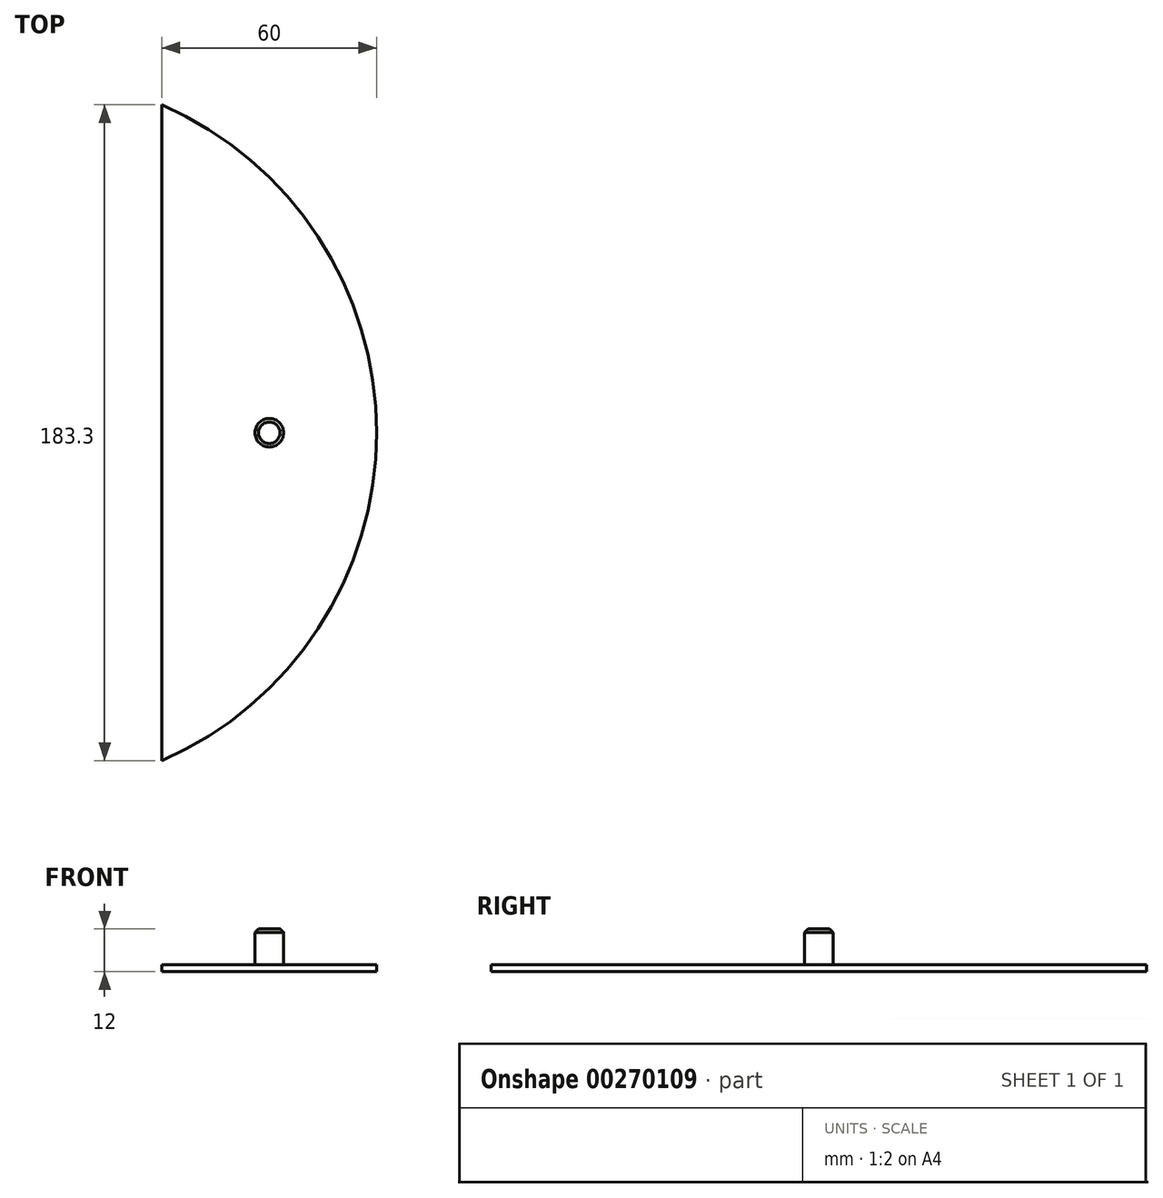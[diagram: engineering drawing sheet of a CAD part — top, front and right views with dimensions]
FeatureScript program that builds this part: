
annotation { "Feature Type Name" : "Feature", "Feature Type Description" : "" }
export const myFeature = defineFeature(function(context is Context, id is Id, definition is map)
    precondition{}
    {
        {
            var Q0;
            Q0=qCreatedBy(makeId("Top.planeOp"),FACE);
            var sketch = newSketch(context, id + "F0", { "sketchPlane" : qUnion([Q0])});
            skLineSegment(sketch, "E0.left", {"start": v(0, -100) * mm, "end": v(0, 100) * mm});
            skPoint(sketch, "E0.middle", {"position": v(0, 0) * mm});
            skArc(sketch, "E1", {"start": v(0, -100) * mm, "mid": v(100, 0) * mm, "end": v(0, 100) * mm});
            skLineSegment(sketch, "E2", {"start": v(40, 91.65) * mm, "end": v(40, -91.65) * mm});
            skSolve(sketch);
        }
        {
            var Q0;
            {var subQ0=sQuery(id+"F0.wireOp",EDGE,"E2");Q0=makeQuery(id+"F0.imprint","IMPRINT",FACE,{"disambiguationData":[TD([[makeQuery(id+"F0.imprint","IMPRINT",EDGE,{"derivedFrom":subQ0}),1.0]])]});}
            extrude(context, id + "F1", {"entities" : qUnion([Q0]), "depth" : 2 * mm});
        }
        {
            var Q0;
            Q0=makeQuery(id+"F1.opExtrude","CAP_FACE",FACE,{"disambiguationData":[OSD([sQuery(id+"F0.wireOp",EDGE,"E0.left"),sQuery(id+"F0.wireOp",EDGE,"E1")])],"isStart":false});
            var sketch = newSketch(context, id + "F2", { "sketchPlane" : qUnion([Q0])});
            skCircle(sketch, "E3", {"center": v(70, 0) * mm, "radius": 4 * mm});
            skPoint(sketch, "E3.centerSnap0", {"position": v(0, 0) * mm});
            skSolve(sketch);
        }
        {
            var Q0;
            Q0=makeQuery(id+"F2.imprint","IMPRINT",FACE,{"disambiguationData":[TD([[makeQuery(id+"F2.imprint","IMPRINT",EDGE,{"derivedFrom":sQuery(id+"F2.wireOp",EDGE,"E3")}),1.0]])]});
            extrude(context, id + "F3", {"entities" : qUnion([Q0]), "operationType" : NewBodyOperationType.ADD, "depth" : 10 * mm});
        }
        {
            var Q0;
            Q0=makeQuery(id+"F3.opExtrude","CAP_EDGE",EDGE,{"disambiguationData":[OSD([sQuery(id+"F2.wireOp",EDGE,"E3")])],"isStart":false});
            chamfer(context, id + "F4", {"entities" : qUnion([Q0]), "width" : 1 * mm, "tangentPropagation" : true});
        }
    });
